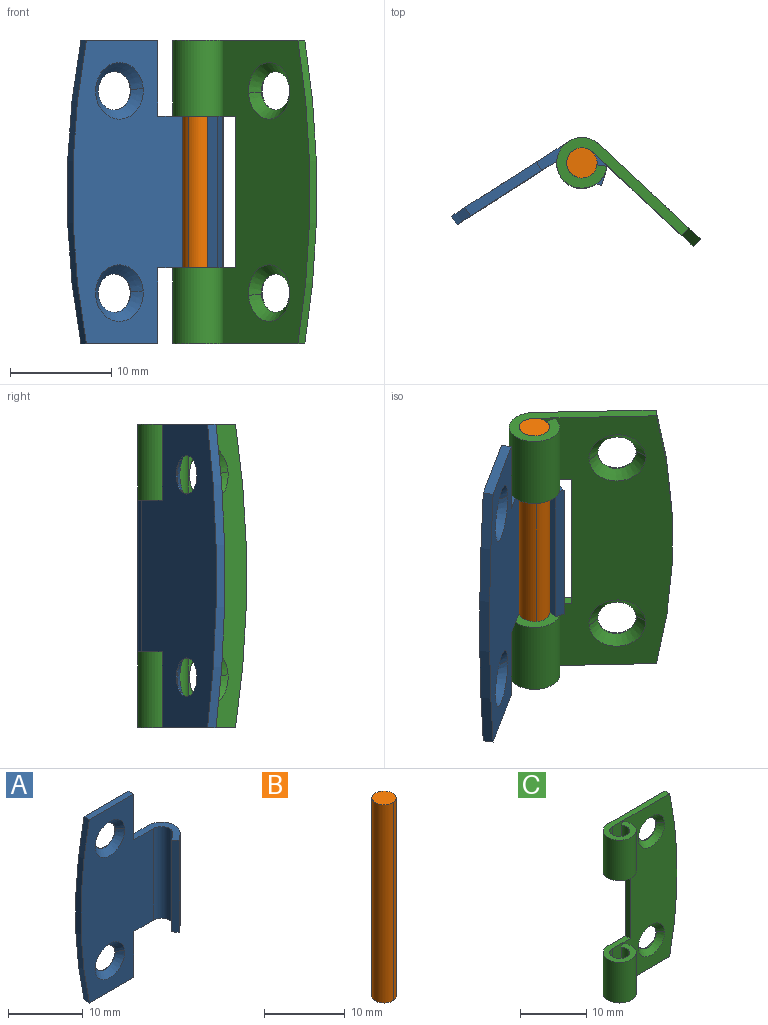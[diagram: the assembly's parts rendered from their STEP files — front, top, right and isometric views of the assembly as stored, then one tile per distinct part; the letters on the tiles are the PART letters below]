
ASSEMBLY  parts=3 mates=4
PART A: 22 faces, bbox 16.3x5.4x30 mm
  f0: cylinder r=1.9mm len=3.78mm, axis (0,1,0), area 0.6mm2, adj f1,f3,f20
  f1: cylinder r=1.9mm len=3.8mm, axis (0,1,0), area 0.6mm2, adj f0,f2,f3,f20
  f2: cone r=1.88mm half-angle=45deg, axis (0,-1,0), area 9.4mm2, adj f1,f3,f21
  f3: cone r=2.38mm half-angle=45deg, axis (0,-1,0), area 9.4mm2, adj f0,f1,f2,f21
  f4: cylinder r=1.9mm len=3.78mm, axis (0,1,0), area 0.6mm2, adj f5,f7,f20
  f5: cylinder r=1.9mm len=3.8mm, axis (0,1,0), area 0.6mm2, adj f4,f6,f7,f20
  f6: cone r=1.88mm half-angle=45deg, axis (0,-1,0), area 9.4mm2, adj f5,f7,f21
  f7: cone r=2.38mm half-angle=45deg, axis (0,-1,0), area 9.4mm2, adj f4,f5,f6,f21
  f8: plane 6.25x5.4mm, normal (0,0,-1), area 10.2mm2, adj f10,f11,f12,f13,f14,f17,f20,f21
  f9: plane 6.25x5.4mm, normal (0,0,1), area 10.2mm2, adj f10,f11,f12,f13,f14,f19,f20,f21
  f10: cylinder r=1.5mm len=15mm, axis (0,0,-1), area 55mm2, adj f8,f9,f11,f21
  f11: plane 15x1.17mm, normal (-0.64,0.77,0), area 23mm2, adj f8,f9,f10,f12
  f12: plane 15x0.77mm, normal (-0.77,-0.64,0), area 15mm2, adj f8,f9,f11,f13
  f13: plane 15x1.17mm, normal (0.64,-0.77,0), area 23mm2, adj f8,f9,f12,f14
  f14: cylinder r=2.5mm len=15mm, axis (0,0,-1), area 91.6mm2, adj f8,f9,f13,f20
  f15: cylinder r=70mm len=30mm, axis (0,1,0), area 30.2mm2, adj f16,f18,f20,f21
  f16: plane 8.37x1mm, normal (0,0,-1), area 8.4mm2, adj f15,f17,f20,f21
  f17: plane 7.5x1mm, normal (1,0,0), area 7.5mm2, adj f8,f16,f20,f21
  f18: plane 8.37x1mm, normal (0,0,1), area 8.4mm2, adj f15,f19,f20,f21
  f19: plane 7.5x1mm, normal (1,0,0), area 7.5mm2, adj f9,f18,f20,f21
  f20: plane 30x13.75mm, normal (0,1,0), area 317.4mm2, adj f0,f1,f4,f5,f8,f9,f14,f15
  f21: plane 30x13.75mm, normal (0,-1,0), area 290.8mm2, adj f2,f3,f6,f7,f8,f9,f10,f15
PART B: 4 faces, bbox 3x3x30 mm
  f0: cylinder r=1.5mm len=30mm, axis (0,0,-1), area 143.9mm2, adj f1,f2,f3
  f1: cylinder r=1.5mm len=30mm, axis (0,0,-1), area 138.8mm2, adj f0,f2,f3
  f2: plane 3x3mm, normal (0,0,-1), area 7.1mm2, adj f0,f1
  f3: plane 3x3mm, normal (0,0,1), area 7.1mm2, adj f0,f1
PART C: 22 faces, bbox 16.3x5x30 mm
  f0: cylinder r=1.9mm len=3.78mm, axis (0,1,0), area 0.6mm2, adj f1,f3,f20
  f1: cylinder r=1.9mm len=3.8mm, axis (0,1,0), area 0.6mm2, adj f0,f2,f3,f20
  f2: cone r=1.88mm half-angle=45deg, axis (0,-1,0), area 9.4mm2, adj f1,f3,f21
  f3: cone r=2.38mm half-angle=45deg, axis (0,-1,0), area 9.4mm2, adj f0,f1,f2,f21
  f4: cylinder r=1.9mm len=3.78mm, axis (0,1,0), area 0.6mm2, adj f5,f7,f20
  f5: cylinder r=1.9mm len=3.8mm, axis (0,1,0), area 0.6mm2, adj f4,f6,f7,f20
  f6: cone r=1.88mm half-angle=45deg, axis (0,-1,0), area 9.4mm2, adj f5,f7,f21
  f7: cone r=2.38mm half-angle=45deg, axis (0,-1,0), area 9.4mm2, adj f4,f5,f6,f21
  f8: plane 7.5x0.81mm, normal (-0.58,0.81,0), area 7.5mm2, adj f9,f10,f14,f19
  f9: cylinder r=1.5mm len=7.5mm, axis (0,0,-1), area 60mm2, adj f8,f14,f19,f21
  f10: cylinder r=2.5mm len=7.5mm, axis (0,0,-1), area 100mm2, adj f8,f14,f19,f20
  f11: plane 7.5x0.81mm, normal (-0.58,0.81,0), area 7.5mm2, adj f12,f13,f16,f17
  f12: cylinder r=1.5mm len=7.5mm, axis (0,0,-1), area 60mm2, adj f11,f16,f17,f21
  f13: cylinder r=2.5mm len=7.5mm, axis (0,0,-1), area 100mm2, adj f11,f16,f17,f20
  f14: plane 6.25x5mm, normal (0,0,-1), area 14.4mm2, adj f8,f9,f10,f15,f20,f21
  f15: plane 15x1mm, normal (-1,0,0), area 15mm2, adj f14,f16,f20,f21
  f16: plane 6.25x5mm, normal (0,0,1), area 14.4mm2, adj f11,f12,f13,f15,f20,f21
  f17: plane 14.62x5mm, normal (0,0,-1), area 22.8mm2, adj f11,f12,f13,f18,f20,f21
  f18: cylinder r=70mm len=30mm, axis (0,1,0), area 30.2mm2, adj f17,f19,f20,f21
  f19: plane 14.62x5mm, normal (0,0,1), area 22.8mm2, adj f8,f9,f10,f18,f20,f21
  f20: plane 30x13.75mm, normal (0,1,0), area 317.4mm2, adj f0,f1,f4,f5,f10,f13,f14,f15
  f21: plane 30x13.75mm, normal (0,-1,0), area 290.8mm2, adj f2,f3,f6,f7,f9,f12,f14,f15
PLACE A rot(axis=(0,0,1),32.5deg) t=(5.26,23.73,23.38)mm
PLACE B rot(axis=(0,0,-1),43deg) t=(5.26,23.73,23.38)mm
PLACE C rot(axis=(0,0,-1),43deg) t=(5.26,23.73,23.38)mm
MATE planar C.f12 <-> B.f0  axis (0,0,-1) through (5.26,23.73,23.38)mm
MATE cylindrical A.f14 <-> C.f10  axis (0,0,1) through (5.26,23.73,45.88)mm
MATE cylindrical B.f1 <-> C.f10  axis (0,0,1) through (5.26,23.73,53.38)mm
MATE planar C.f10 <-> A.f14  axis (0,0,-1) through (5.26,23.73,45.88)mm
